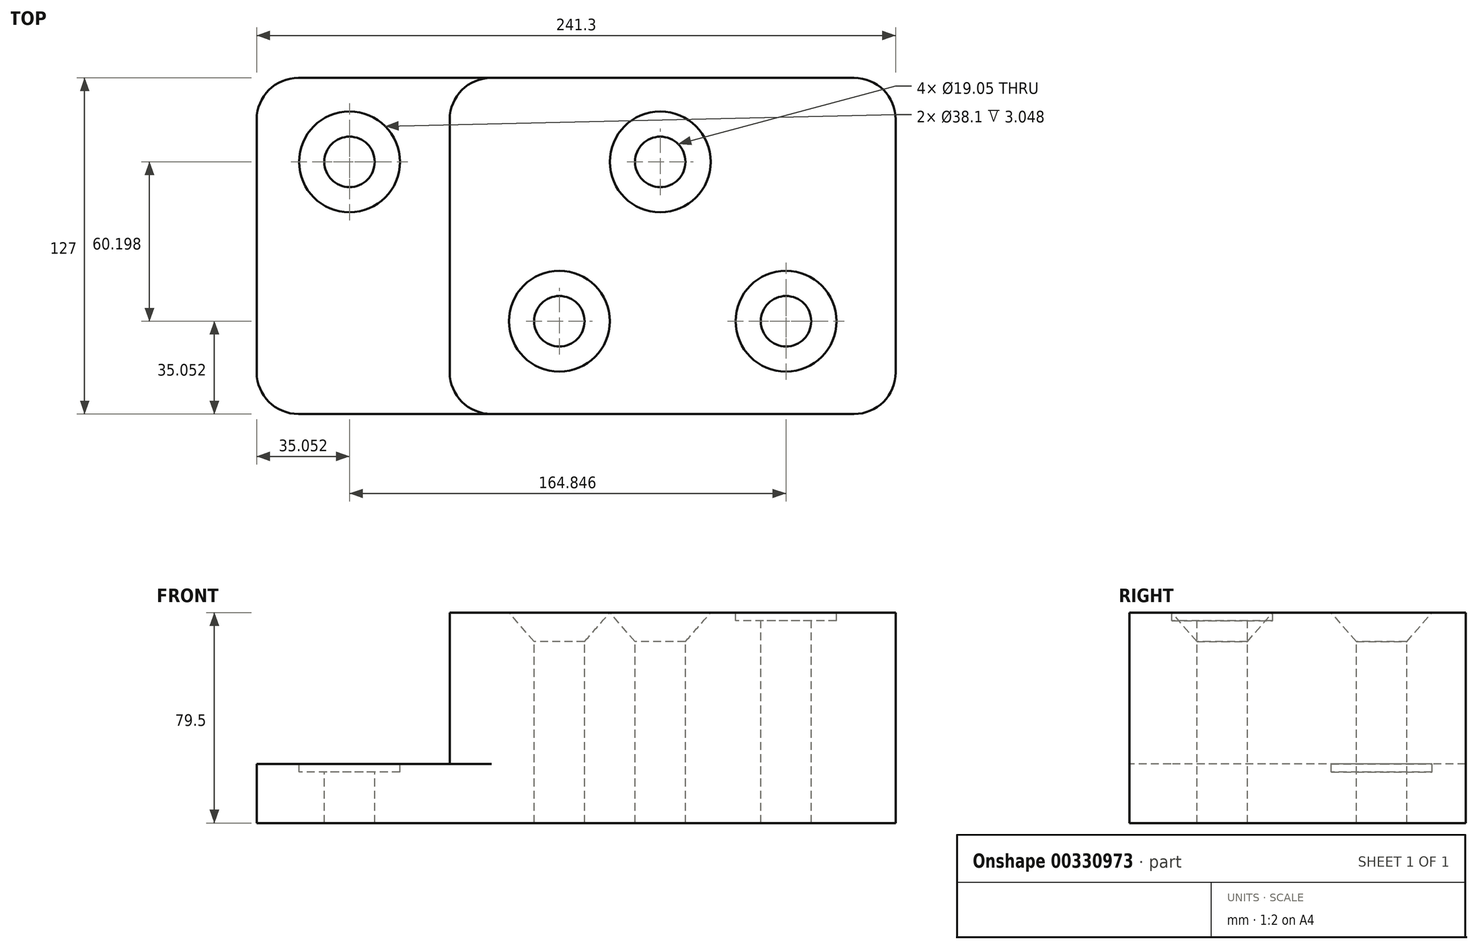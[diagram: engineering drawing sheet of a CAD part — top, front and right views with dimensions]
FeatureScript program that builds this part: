
annotation { "Feature Type Name" : "Feature", "Feature Type Description" : "" }
export const myFeature = defineFeature(function(context is Context, id is Id, definition is map)
    precondition{}
    {
        {
            var Q0;
            Q0=qCreatedBy(makeId("Top.planeOp"),FACE);
            var sketch = newSketch(context, id + "F0", { "sketchPlane" : qUnion([Q0])});
            skLineSegment(sketch, "E0.bottom", {"start": v(-98.55, 63.5) * mm, "end": v(111.25, 63.5) * mm});
            skLineSegment(sketch, "E0.top", {"start": v(-98.55, -63.5) * mm, "end": v(111.25, -63.5) * mm});
            skLineSegment(sketch, "E0.left", {"start": v(-114.3, 47.75) * mm, "end": v(-114.3, -47.75) * mm});
            skLineSegment(sketch, "E0.right", {"start": v(127, 47.75) * mm, "end": v(127, -47.75) * mm});
            skPoint(sketch, "E1.visualSharp", {"position": v(-114.3, 63.5) * mm});
            skArc(sketch, "E1.filletArc", {"start": v(-98.55, 63.5) * mm, "mid": v(-109.69, 58.89) * mm, "end": v(-114.3, 47.75) * mm});
            skPoint(sketch, "E2.visualSharp", {"position": v(-114.3, -63.5) * mm});
            skArc(sketch, "E2.filletArc", {"start": v(-114.3, -47.75) * mm, "mid": v(-109.69, -58.89) * mm, "end": v(-98.55, -63.5) * mm});
            skPoint(sketch, "E3.visualSharp", {"position": v(127, -63.5) * mm});
            skArc(sketch, "E3.filletArc", {"start": v(111.25, -63.5) * mm, "mid": v(122.39, -58.89) * mm, "end": v(127, -47.75) * mm});
            skPoint(sketch, "E4.visualSharp", {"position": v(127, 63.5) * mm});
            skArc(sketch, "E4.filletArc", {"start": v(127, 47.75) * mm, "mid": v(122.39, 58.89) * mm, "end": v(111.25, 63.5) * mm});
            skSolve(sketch);
        }
        {
            var Q0;
            Q0 = qSketchRegion(id + "F0", true);
            extrude(context, id + "F1", {"entities" : qUnion([Q0]), "depth" : 22.35 * mm});
        }
        {
            var Q0;
            Q0=makeQuery(id+"F1.opExtrude","CAP_FACE",FACE,{"disambiguationData":[OSD([sQuery(id+"F0.wireOp",EDGE,"E0.bottom"),sQuery(id+"F0.wireOp",EDGE,"E0.top"),sQuery(id+"F0.wireOp",EDGE,"E0.left"),sQuery(id+"F0.wireOp",EDGE,"E0.right"),sQuery(id+"F0.wireOp",EDGE,"E1.filletArc"),sQuery(id+"F0.wireOp",EDGE,"E2.filletArc"),sQuery(id+"F0.wireOp",EDGE,"E3.filletArc"),sQuery(id+"F0.wireOp",EDGE,"E4.filletArc")])],"isStart":false});
            var sketch = newSketch(context, id + "F2", { "sketchPlane" : qUnion([Q0])});
            skLineSegment(sketch, "E5.bottom", {"start": v(111.25, -63.5) * mm, "end": v(-25.65, -63.5) * mm});
            skLineSegment(sketch, "E5.top", {"start": v(111.25, 63.5) * mm, "end": v(-25.65, 63.5) * mm});
            skLineSegment(sketch, "E5.left", {"start": v(127, -47.75) * mm, "end": v(127, 47.75) * mm});
            skLineSegment(sketch, "E5.right", {"start": v(-41.4, -47.75) * mm, "end": v(-41.4, 47.75) * mm});
            skPoint(sketch, "E6.visualSharp", {"position": v(-41.4, 63.5) * mm});
            skArc(sketch, "E6.filletArc", {"start": v(-25.65, 63.5) * mm, "mid": v(-36.79, 58.89) * mm, "end": v(-41.4, 47.75) * mm});
            skPoint(sketch, "E7.visualSharp", {"position": v(127, 63.5) * mm});
            skArc(sketch, "E7.filletArc", {"start": v(127, 47.75) * mm, "mid": v(122.39, 58.89) * mm, "end": v(111.25, 63.5) * mm});
            skPoint(sketch, "E8.visualSharp", {"position": v(127, -63.5) * mm});
            skArc(sketch, "E8.filletArc", {"start": v(111.25, -63.5) * mm, "mid": v(122.39, -58.89) * mm, "end": v(127, -47.75) * mm});
            skPoint(sketch, "E9.visualSharp", {"position": v(-41.4, -63.5) * mm});
            skArc(sketch, "E9.filletArc", {"start": v(-41.4, -47.75) * mm, "mid": v(-36.79, -58.89) * mm, "end": v(-25.65, -63.5) * mm});
            skSolve(sketch);
        }
        {
            var Q0;
            Q0=makeQuery(id+"F2.imprint","IMPRINT",FACE,{"disambiguationData":[TD([[makeQuery(id+"F2.imprint","IMPRINT",EDGE,{"derivedFrom":sQuery(id+"F2.wireOp",EDGE,"E5.bottom")}),1.0]])]});
            extrude(context, id + "F3", {"entities" : qUnion([Q0]), "operationType" : NewBodyOperationType.ADD, "depth" : 57.15 * mm});
        }
        {
            var Q0;
            Q0=makeQuery(id+"F1.opExtrude","CAP_FACE",FACE,{"disambiguationData":[OSD([sQuery(id+"F0.wireOp",EDGE,"E0.bottom"),sQuery(id+"F0.wireOp",EDGE,"E0.top"),sQuery(id+"F0.wireOp",EDGE,"E0.left"),sQuery(id+"F0.wireOp",EDGE,"E0.right"),sQuery(id+"F0.wireOp",EDGE,"E1.filletArc"),sQuery(id+"F0.wireOp",EDGE,"E2.filletArc"),sQuery(id+"F0.wireOp",EDGE,"E3.filletArc"),sQuery(id+"F0.wireOp",EDGE,"E4.filletArc")])],"isStart":false});
            var sketch = newSketch(context, id + "F4", { "sketchPlane" : qUnion([Q0])});
            skPoint(sketch, "E10", {"position": v(-79.25, 31.75) * mm});
            skPoint(sketch, "E11", {"position": v(38.1, 31.75) * mm});
            skPoint(sketch, "E12", {"position": v(0, -28.45) * mm});
            skPoint(sketch, "E13", {"position": v(85.6, -28.45) * mm});
            skSolve(sketch);
        }
        {
            var Q0;
            Q0=sQuery(id+"F4.wireOp",VERTEX,"E10");
            var Q1;
            Q1=makeQuery(id+"F1.opExtrude","SWEPT_BODY",BODY,{"disambiguationData":[OSD([sQuery(id+"F0.wireOp",EDGE,"E0.bottom"),sQuery(id+"F0.wireOp",EDGE,"E0.top"),sQuery(id+"F0.wireOp",EDGE,"E0.left"),sQuery(id+"F0.wireOp",EDGE,"E0.right"),sQuery(id+"F0.wireOp",EDGE,"E1.filletArc"),sQuery(id+"F0.wireOp",EDGE,"E2.filletArc"),sQuery(id+"F0.wireOp",EDGE,"E3.filletArc"),sQuery(id+"F0.wireOp",EDGE,"E4.filletArc")])]});
            hole(context, id + "F5", {"style" : HoleStyle.C_BORE, "endStyle" : HoleEndStyle.THROUGH, "holeDiameter" : 19.05 * mm, "cBoreDiameter" : 38.1 * mm, "cBoreDepth" : 3.05 * mm, "tappedDepth" : 12.7 * mm, "tapClearance" : 3, "locations" : qUnion([Q0]), "scope" : qUnion([Q1])});
        }
        {
            var Q0;
            Q0=makeQuery(id+"F3.opExtrude","CAP_FACE",FACE,{"disambiguationData":[OSD([sQuery(id+"F2.wireOp",EDGE,"E5.bottom"),sQuery(id+"F2.wireOp",EDGE,"E5.top"),sQuery(id+"F2.wireOp",EDGE,"E5.left"),sQuery(id+"F2.wireOp",EDGE,"E5.right"),sQuery(id+"F2.wireOp",EDGE,"E6.filletArc"),sQuery(id+"F2.wireOp",EDGE,"E7.filletArc"),sQuery(id+"F2.wireOp",EDGE,"E8.filletArc"),sQuery(id+"F2.wireOp",EDGE,"E9.filletArc")])],"isStart":false});
            var sketch = newSketch(context, id + "F6", { "sketchPlane" : qUnion([Q0])});
            skPoint(sketch, "E14", {"position": v(38.1, 31.75) * mm});
            skPoint(sketch, "E15", {"position": v(0, -28.45) * mm});
            skPoint(sketch, "E16", {"position": v(85.6, -28.45) * mm});
            skSolve(sketch);
        }
        {
            var Q0;
            Q0=sQuery(id+"F6.wireOp",VERTEX,"E16");
            var Q1;
            Q1=makeQuery(id+"F1.opExtrude","SWEPT_BODY",BODY,{"disambiguationData":[OSD([sQuery(id+"F0.wireOp",EDGE,"E0.bottom"),sQuery(id+"F0.wireOp",EDGE,"E0.top"),sQuery(id+"F0.wireOp",EDGE,"E0.left"),sQuery(id+"F0.wireOp",EDGE,"E0.right"),sQuery(id+"F0.wireOp",EDGE,"E1.filletArc"),sQuery(id+"F0.wireOp",EDGE,"E2.filletArc"),sQuery(id+"F0.wireOp",EDGE,"E3.filletArc"),sQuery(id+"F0.wireOp",EDGE,"E4.filletArc")])]});
            hole(context, id + "F7", {"style" : HoleStyle.C_BORE, "endStyle" : HoleEndStyle.THROUGH, "holeDiameter" : 19.05 * mm, "cBoreDiameter" : 38.1 * mm, "cBoreDepth" : 3.05 * mm, "tappedDepth" : 12.7 * mm, "tapClearance" : 3, "locations" : qUnion([Q0]), "scope" : qUnion([Q1])});
        }
        {
            var Q0;
            Q0=sQuery(id+"F6.wireOp",VERTEX,"E14");
            var Q1;
            Q1=sQuery(id+"F6.wireOp",VERTEX,"E15");
            var Q2;
            Q2=makeQuery(id+"F1.opExtrude","SWEPT_BODY",BODY,{"disambiguationData":[OSD([sQuery(id+"F0.wireOp",EDGE,"E0.bottom"),sQuery(id+"F0.wireOp",EDGE,"E0.top"),sQuery(id+"F0.wireOp",EDGE,"E0.left"),sQuery(id+"F0.wireOp",EDGE,"E0.right"),sQuery(id+"F0.wireOp",EDGE,"E1.filletArc"),sQuery(id+"F0.wireOp",EDGE,"E2.filletArc"),sQuery(id+"F0.wireOp",EDGE,"E3.filletArc"),sQuery(id+"F0.wireOp",EDGE,"E4.filletArc")])]});
            hole(context, id + "F8", {"style" : HoleStyle.C_SINK, "endStyle" : HoleEndStyle.THROUGH, "holeDiameter" : 19.05 * mm, "cSinkDiameter" : 38.1 * mm, "cSinkAngle" : 82 * degree, "tappedDepth" : 12.7 * mm, "tapClearance" : 3, "locations" : qUnion([Q0, Q1]), "scope" : qUnion([Q2])});
        }
    });
